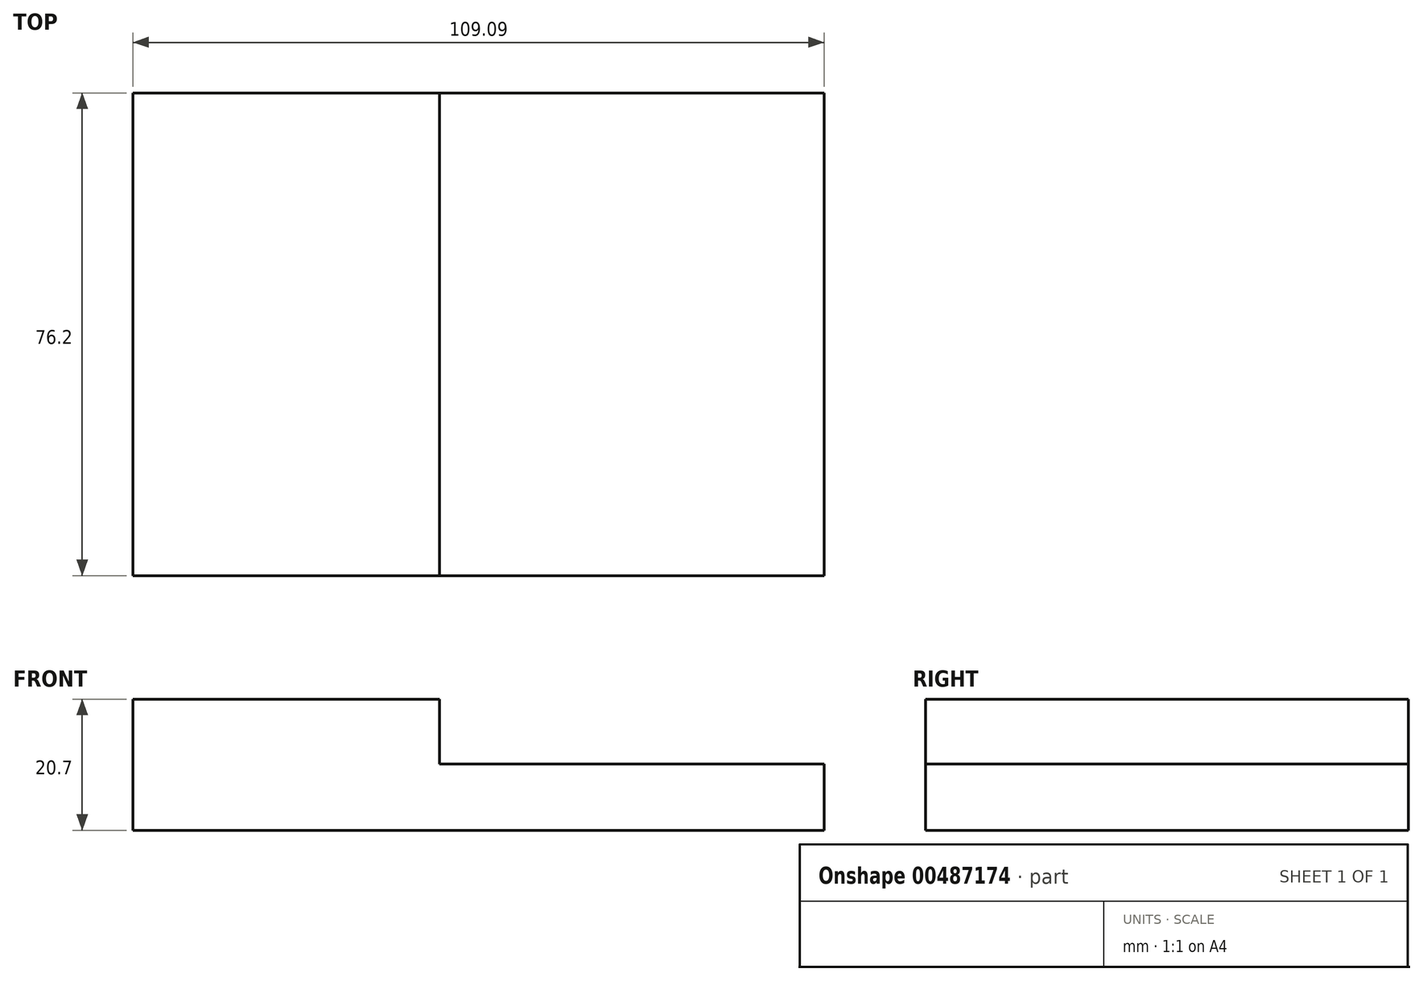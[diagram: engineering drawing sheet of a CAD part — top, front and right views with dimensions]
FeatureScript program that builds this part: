
annotation { "Feature Type Name" : "Feature", "Feature Type Description" : "" }
export const myFeature = defineFeature(function(context is Context, id is Id, definition is map)
    precondition{}
    {
        {
            var Q0;
            Q0=qCreatedBy(makeId("Front.planeOp"),FACE);
            var sketch = newSketch(context, id + "F0", { "sketchPlane" : qUnion([Q0])});
            skLineSegment(sketch, "E0", {"start": v(-67.45, 43.03) * mm, "end": v(-19.08, 43.03) * mm});
            skLineSegment(sketch, "E1", {"start": v(-19.08, 43.03) * mm, "end": v(-19.08, 32.8) * mm});
            skLineSegment(sketch, "E2", {"start": v(-19.08, 32.8) * mm, "end": v(41.64, 32.8) * mm});
            skLineSegment(sketch, "E3", {"start": v(41.64, 32.8) * mm, "end": v(41.64, 22.33) * mm});
            skLineSegment(sketch, "E4", {"start": v(41.64, 22.33) * mm, "end": v(-67.45, 22.33) * mm});
            skLineSegment(sketch, "E5", {"start": v(-67.45, 22.33) * mm, "end": v(-67.45, 43.03) * mm});
            skSolve(sketch);
        }
        {
            var Q0;
            Q0 = qSketchRegion(id + "F0", true);
            extrude(context, id + "F1", {"entities" : qUnion([Q0]), "depth" : 76.2 * mm});
        }
    });
